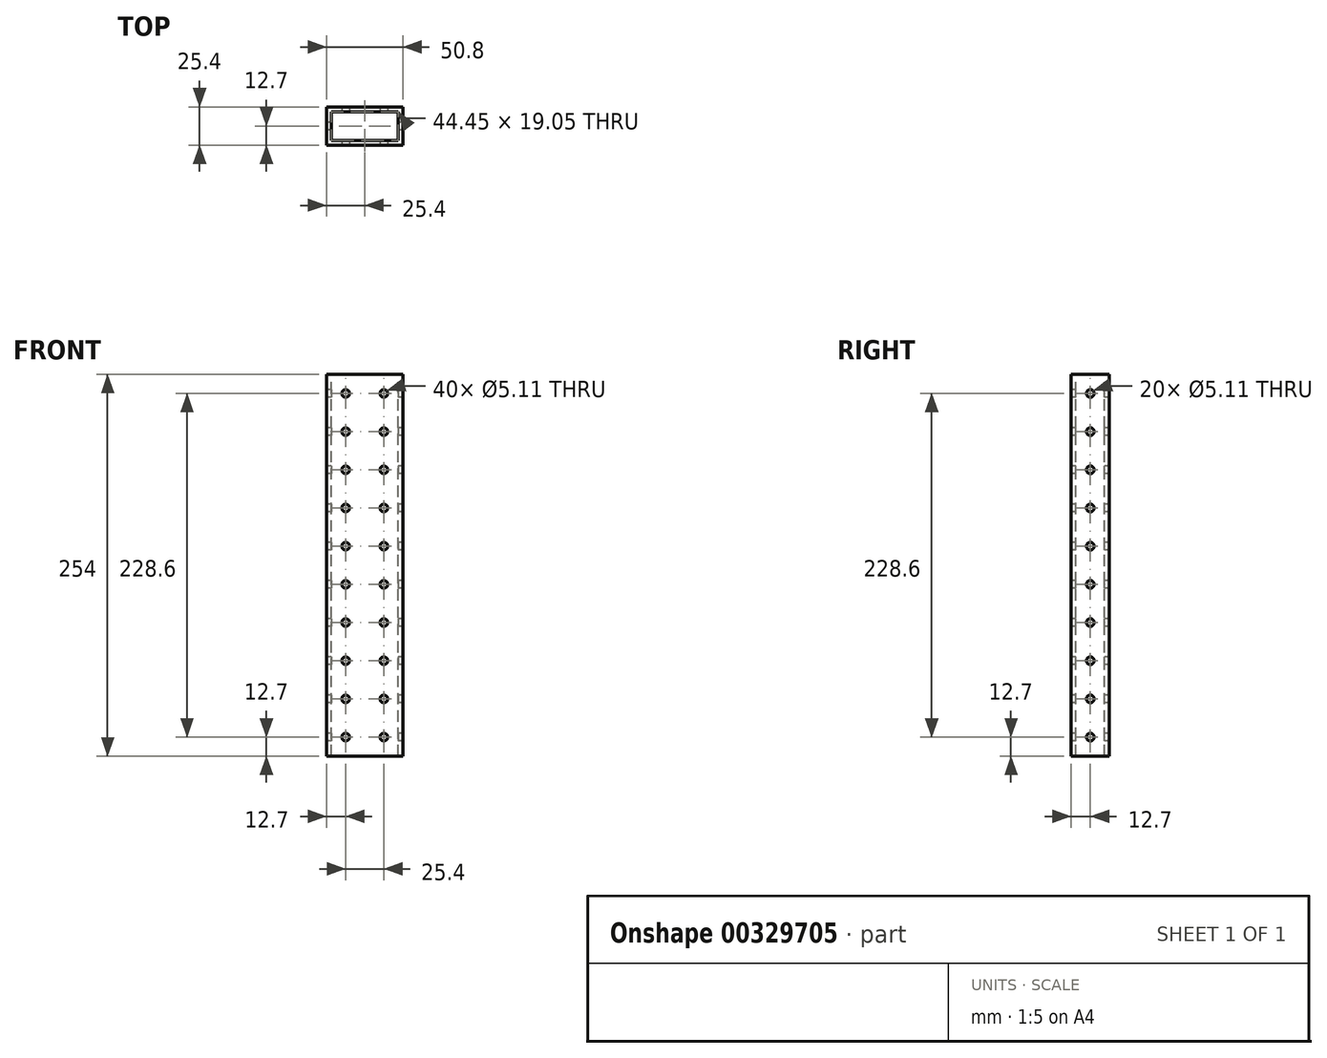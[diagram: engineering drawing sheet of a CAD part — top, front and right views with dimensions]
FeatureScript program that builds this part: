
annotation { "Feature Type Name" : "Feature", "Feature Type Description" : "" }
export const myFeature = defineFeature(function(context is Context, id is Id, definition is map)
    precondition{}
    {
        {
            var Q0;
            Q0=qCreatedBy(makeId("Top.planeOp"),FACE);
            var sketch = newSketch(context, id + "F0", { "sketchPlane" : qUnion([Q0])});
            skLineSegment(sketch, "E0.bottom", {"start": v(-25.54, 76.66) * mm, "end": v(25.26, 76.66) * mm});
            skLineSegment(sketch, "E0.top", {"start": v(-25.54, 51.26) * mm, "end": v(25.26, 51.26) * mm});
            skLineSegment(sketch, "E0.left", {"start": v(-25.54, 76.66) * mm, "end": v(-25.54, 51.26) * mm});
            skLineSegment(sketch, "E0.right", {"start": v(25.26, 76.66) * mm, "end": v(25.26, 51.26) * mm});
            skSolve(sketch);
        }
        {
            var Q0;
            Q0 = qSketchRegion(id + "F0", true);
            extrude(context, id + "F1", {"entities" : qUnion([Q0]), "depth" : 254 * mm});
        }
        {
            var Q0;
            Q0=makeQuery(id+"F1.opExtrude","SWEPT_FACE",FACE,{"disambiguationData":[OSD([sQuery(id+"F0.wireOp",EDGE,"E0.top")])]});
            var sketch = newSketch(context, id + "F2", { "sketchPlane" : qUnion([Q0])});
            skCircle(sketch, "E1", {"center": v(-12.84, 241.3) * mm, "radius": 2.55 * mm});
            skCircle(sketch, "E2.0.1.0", {"center": v(-12.84, 215.9) * mm, "radius": 2.55 * mm});
            skCircle(sketch, "E2.0.2.0", {"center": v(-12.84, 190.5) * mm, "radius": 2.55 * mm});
            skCircle(sketch, "E2.0.3.0", {"center": v(-12.84, 165.1) * mm, "radius": 2.55 * mm});
            skCircle(sketch, "E2.0.4.0", {"center": v(-12.84, 139.7) * mm, "radius": 2.55 * mm});
            skCircle(sketch, "E2.0.5.0", {"center": v(-12.84, 114.3) * mm, "radius": 2.55 * mm});
            skCircle(sketch, "E2.0.6.0", {"center": v(-12.84, 88.9) * mm, "radius": 2.55 * mm});
            skCircle(sketch, "E2.0.7.0", {"center": v(-12.84, 63.5) * mm, "radius": 2.55 * mm});
            skCircle(sketch, "E2.0.8.0", {"center": v(-12.84, 38.1) * mm, "radius": 2.55 * mm});
            skCircle(sketch, "E2.0.9.0", {"center": v(-12.84, 12.7) * mm, "radius": 2.55 * mm});
            skCircle(sketch, "E2.1.0.0", {"center": v(12.56, 241.3) * mm, "radius": 2.55 * mm});
            skCircle(sketch, "E2.1.1.0", {"center": v(12.56, 215.9) * mm, "radius": 2.55 * mm});
            skCircle(sketch, "E2.1.2.0", {"center": v(12.56, 190.5) * mm, "radius": 2.55 * mm});
            skCircle(sketch, "E2.1.3.0", {"center": v(12.56, 165.1) * mm, "radius": 2.55 * mm});
            skCircle(sketch, "E2.1.4.0", {"center": v(12.56, 139.7) * mm, "radius": 2.55 * mm});
            skCircle(sketch, "E2.1.5.0", {"center": v(12.56, 114.3) * mm, "radius": 2.55 * mm});
            skCircle(sketch, "E2.1.6.0", {"center": v(12.56, 88.9) * mm, "radius": 2.55 * mm});
            skCircle(sketch, "E2.1.7.0", {"center": v(12.56, 63.5) * mm, "radius": 2.55 * mm});
            skCircle(sketch, "E2.1.8.0", {"center": v(12.56, 38.1) * mm, "radius": 2.55 * mm});
            skCircle(sketch, "E2.1.9.0", {"center": v(12.56, 12.7) * mm, "radius": 2.55 * mm});
            skLineSegment(sketch, "E2.direction1", {"start": v(-12.84, 241.3) * mm, "end": v(12.56, 241.3) * mm, "construction": true});
            skLineSegment(sketch, "E2.direction2", {"start": v(-12.84, 241.3) * mm, "end": v(-12.84, 215.9) * mm, "construction": true});
            skSolve(sketch);
        }
        {
            var Q0;
            Q0 = qSketchRegion(id + "F2", true);
            extrude(context, id + "F3", {"entities" : qUnion([Q0]), "operationType" : NewBodyOperationType.REMOVE, "oppositeDirection" : true, "depth" : 50.8 * mm});
        }
        {
            var Q0;
            Q0=makeQuery(id+"F1.opExtrude","SWEPT_FACE",FACE,{"disambiguationData":[OSD([sQuery(id+"F0.wireOp",EDGE,"E0.left")])]});
            var sketch = newSketch(context, id + "F4", { "sketchPlane" : qUnion([Q0])});
            skCircle(sketch, "E3", {"center": v(-63.96, 241.3) * mm, "radius": 2.55 * mm});
            skCircle(sketch, "E4.0.1.0", {"center": v(-63.96, 215.9) * mm, "radius": 2.55 * mm});
            skCircle(sketch, "E4.0.2.0", {"center": v(-63.96, 190.5) * mm, "radius": 2.55 * mm});
            skCircle(sketch, "E4.0.3.0", {"center": v(-63.96, 165.1) * mm, "radius": 2.55 * mm});
            skCircle(sketch, "E4.0.4.0", {"center": v(-63.96, 139.7) * mm, "radius": 2.55 * mm});
            skCircle(sketch, "E4.0.5.0", {"center": v(-63.96, 114.3) * mm, "radius": 2.55 * mm});
            skCircle(sketch, "E4.0.6.0", {"center": v(-63.96, 88.9) * mm, "radius": 2.55 * mm});
            skCircle(sketch, "E4.0.7.0", {"center": v(-63.96, 63.5) * mm, "radius": 2.55 * mm});
            skCircle(sketch, "E4.0.8.0", {"center": v(-63.96, 38.1) * mm, "radius": 2.55 * mm});
            skCircle(sketch, "E4.0.9.0", {"center": v(-63.96, 12.7) * mm, "radius": 2.55 * mm});
            skLineSegment(sketch, "E4.direction1", {"start": v(-63.96, 241.3) * mm, "end": v(-38.56, 241.3) * mm, "construction": true});
            skLineSegment(sketch, "E4.direction2", {"start": v(-63.96, 241.3) * mm, "end": v(-63.96, 215.9) * mm, "construction": true});
            skSolve(sketch);
        }
        {
            var Q0;
            Q0 = qSketchRegion(id + "F4", true);
            extrude(context, id + "F5", {"entities" : qUnion([Q0]), "operationType" : NewBodyOperationType.REMOVE, "oppositeDirection" : true, "depth" : 50.8 * mm});
        }
        {
            var Q0;
            Q0=makeQuery(id+"F1.opExtrude","CAP_FACE",FACE,{"disambiguationData":[OSD([sQuery(id+"F0.wireOp",EDGE,"E0.bottom"),sQuery(id+"F0.wireOp",EDGE,"E0.top"),sQuery(id+"F0.wireOp",EDGE,"E0.left"),sQuery(id+"F0.wireOp",EDGE,"E0.right")])],"isStart":false});
            var sketch = newSketch(context, id + "F6", { "sketchPlane" : qUnion([Q0])});
            skLineSegment(sketch, "E5.bottom", {"start": v(-22.37, 73.48) * mm, "end": v(22.08, 73.48) * mm});
            skLineSegment(sketch, "E5.top", {"start": v(-22.37, 54.43) * mm, "end": v(22.08, 54.43) * mm});
            skLineSegment(sketch, "E5.left", {"start": v(-22.37, 73.48) * mm, "end": v(-22.37, 54.43) * mm});
            skLineSegment(sketch, "E5.right", {"start": v(22.08, 73.48) * mm, "end": v(22.08, 54.43) * mm});
            skSolve(sketch);
        }
        {
            var Q0;
            Q0 = qSketchRegion(id + "F6", true);
            extrude(context, id + "F7", {"entities" : qUnion([Q0]), "operationType" : NewBodyOperationType.REMOVE, "oppositeDirection" : true, "depth" : 254 * mm});
        }
    });
